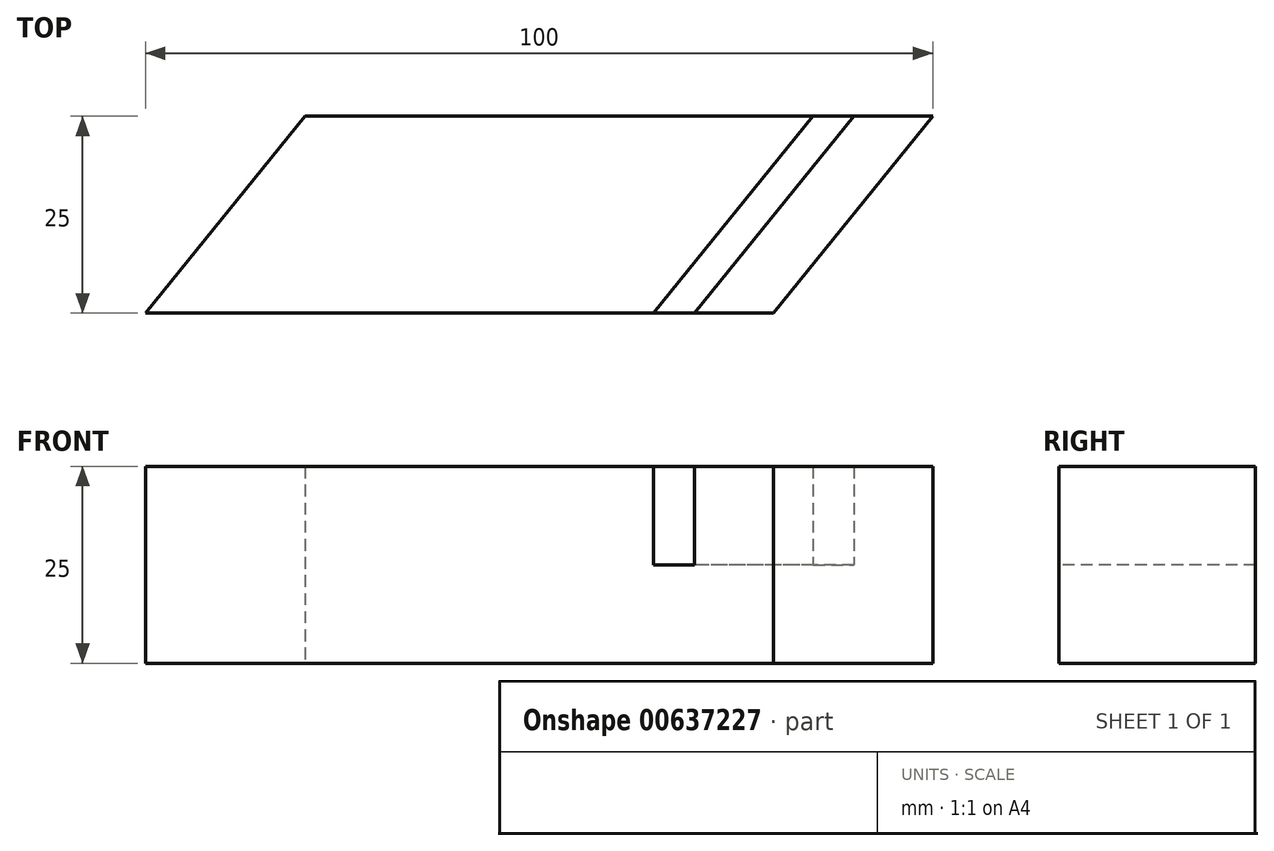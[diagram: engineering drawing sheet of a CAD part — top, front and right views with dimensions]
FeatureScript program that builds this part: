
annotation { "Feature Type Name" : "Feature", "Feature Type Description" : "" }
export const myFeature = defineFeature(function(context is Context, id is Id, definition is map)
    precondition{}
    {
        {
            var Q0;
            Q0=qCreatedBy(makeId("Top.planeOp"),FACE);
            var sketch = newSketch(context, id + "F0", { "sketchPlane" : qUnion([Q0])});
            skLineSegment(sketch, "E0", {"start": v(-45.72, 0) * mm, "end": v(-25.45, 25) * mm});
            skLineSegment(sketch, "E1", {"start": v(-25.45, 25) * mm, "end": v(54.28, 25) * mm});
            skLineSegment(sketch, "E2", {"start": v(54.28, 25) * mm, "end": v(34, 0) * mm});
            skLineSegment(sketch, "E3", {"start": v(34, 0) * mm, "end": v(-45.72, 0) * mm});
            skLineSegment(sketch, "E4", {"start": v(44.28, 25) * mm, "end": v(24, 0) * mm});
            skLineSegment(sketch, "E5", {"start": v(39.08, 25) * mm, "end": v(18.8, 0) * mm});
            skSolve(sketch);
        }
        {
            var Q0;
            {var subQ0=sQuery(id+"F0.wireOp",EDGE,"E0");Q0=makeQuery(id+"F0.imprint","IMPRINT",FACE,{"disambiguationData":[TD([[makeQuery(id+"F0.imprint","IMPRINT",EDGE,{"derivedFrom":subQ0}),-1.0]])]});}
            var Q1;
            {var subQ0=sQuery(id+"F0.wireOp",EDGE,"E2");Q1=makeQuery(id+"F0.imprint","IMPRINT",FACE,{"disambiguationData":[TD([[makeQuery(id+"F0.imprint","IMPRINT",EDGE,{"derivedFrom":subQ0}),-1.0]])]});}
            extrude(context, id + "F1", {"entities" : qUnion([Q0, Q1]), "depth" : 25 * mm, "offsetDistance" : 25 * mm});
        }
        {
            var Q0;
            {var subQ0=sQuery(id+"F0.wireOp",EDGE,"E4");Q0=makeQuery(id+"F0.imprint","IMPRINT",FACE,{"disambiguationData":[TD([[makeQuery(id+"F0.imprint","IMPRINT",EDGE,{"derivedFrom":subQ0}),-1.0]])]});}
            extrude(context, id + "F2", {"entities" : qUnion([Q0]), "operationType" : NewBodyOperationType.ADD, "depth" : 12.5 * mm, "offsetDistance" : 25 * mm});
        }
    });
